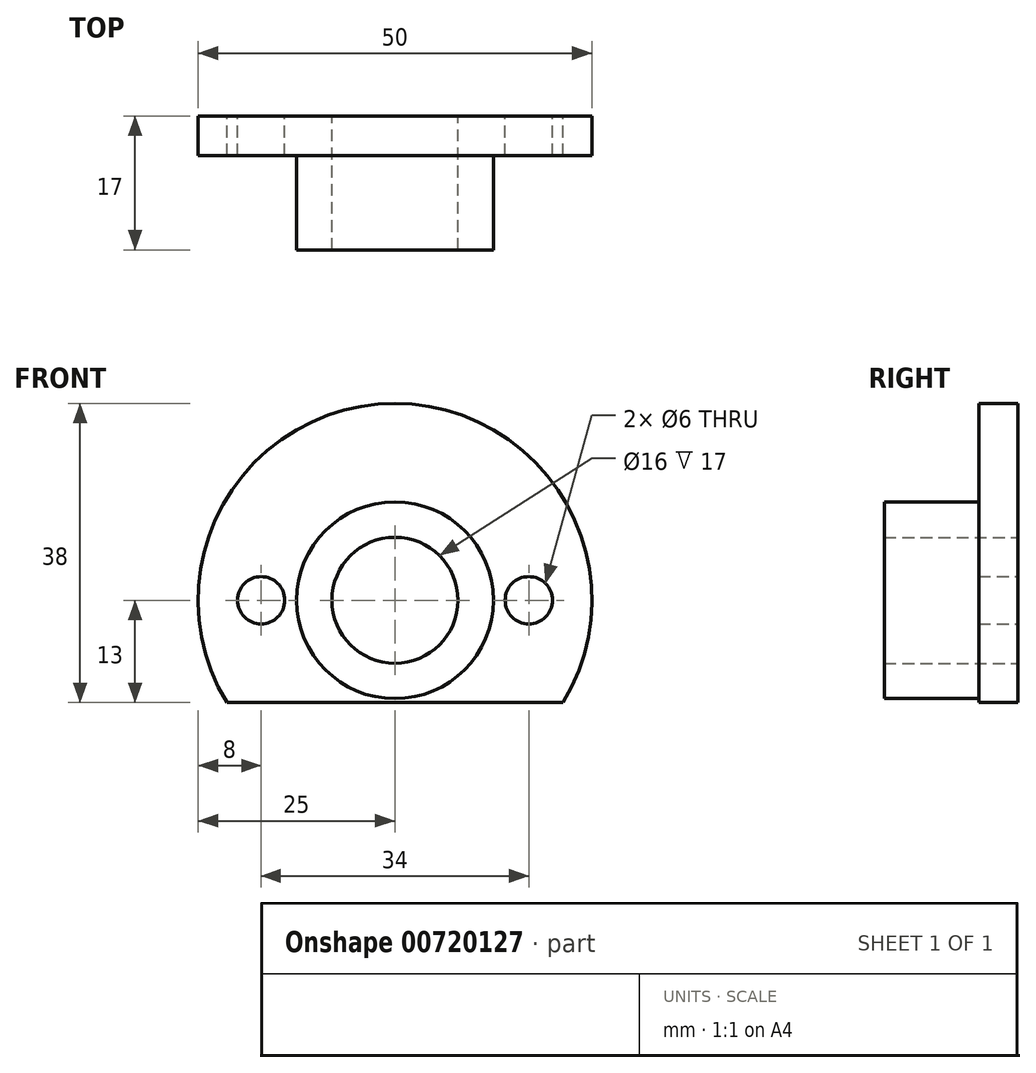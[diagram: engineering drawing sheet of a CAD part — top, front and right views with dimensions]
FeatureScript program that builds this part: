
annotation { "Feature Type Name" : "Feature", "Feature Type Description" : "" }
export const myFeature = defineFeature(function(context is Context, id is Id, definition is map)
    precondition{}
    {
        {
            var Q0;
            Q0=qCreatedBy(makeId("Front.planeOp"),FACE);
            var sketch = newSketch(context, id + "F0", { "sketchPlane" : qUnion([Q0])});
            skArc(sketch, "E0", {"start": v(21.35, -13) * mm, "mid": v(0, 25) * mm, "end": v(-21.35, -13) * mm});
            skCircle(sketch, "E1", {"center": v(0, 0) * mm, "radius": 8 * mm});
            skCircle(sketch, "E2", {"center": v(-17, 0) * mm, "radius": 3 * mm});
            skCircle(sketch, "E3", {"center": v(17, 0) * mm, "radius": 3 * mm});
            skLineSegment(sketch, "E4", {"start": v(-21.35, -13) * mm, "end": v(21.35, -13) * mm});
            skSolve(sketch);
        }
        {
            var Q0;
            Q0=makeQuery(id+"F0.imprint","IMPRINT",FACE,{"disambiguationData":[TD([[makeQuery(id+"F0.imprint","IMPRINT",EDGE,{"derivedFrom":sQuery(id+"F0.wireOp",EDGE,"E0")}),1.0]])]});
            extrude(context, id + "F1", {"entities" : qUnion([Q0]), "depth" : 5 * mm, "offsetDistance" : 25 * mm});
        }
        {
            var Q0;
            Q0=makeQuery(id+"F1.opExtrude","CAP_FACE",FACE,{"disambiguationData":[OSD([sQuery(id+"F0.wireOp",EDGE,"E0"),sQuery(id+"F0.wireOp",EDGE,"E1"),sQuery(id+"F0.wireOp",EDGE,"E2"),sQuery(id+"F0.wireOp",EDGE,"E3"),sQuery(id+"F0.wireOp",EDGE,"E4")])],"isStart":false});
            var sketch = newSketch(context, id + "F2", { "sketchPlane" : qUnion([Q0])});
            skCircle(sketch, "E5", {"center": v(0, 0) * mm, "radius": 12.5 * mm});
            skSolve(sketch);
        }
        {
            var Q0;
            Q0=makeQuery(id+"F2.imprint","IMPRINT",FACE,{"disambiguationData":[TD([[makeQuery(id+"F2.imprint","IMPRINT",EDGE,{"derivedFrom":sQuery(id+"F2.wireOp",EDGE,"E5")}),1.0]])]});
            extrude(context, id + "F3", {"entities" : qUnion([Q0]), "operationType" : NewBodyOperationType.ADD, "depth" : 12 * mm, "offsetDistance" : 25 * mm});
        }
    });
